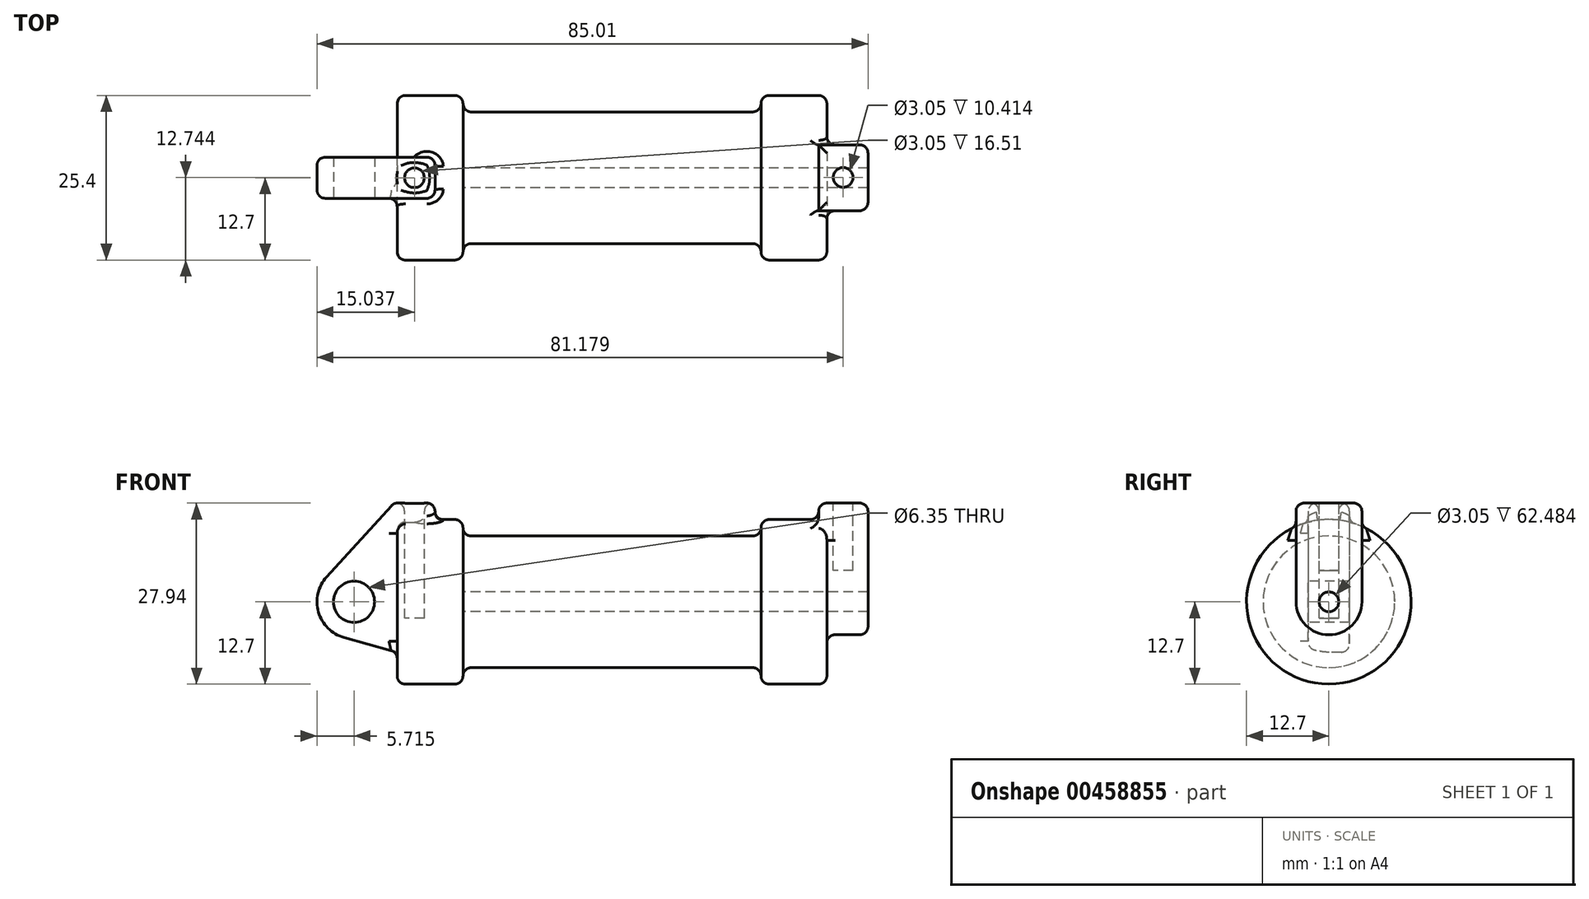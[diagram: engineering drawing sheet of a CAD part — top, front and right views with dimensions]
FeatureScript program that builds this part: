
annotation { "Feature Type Name" : "Feature", "Feature Type Description" : "" }
export const myFeature = defineFeature(function(context is Context, id is Id, definition is map)
    precondition{}
    {
        {
            var Q0;
            Q0=qCreatedBy(makeId("Front.planeOp"),FACE);
            var sketch = newSketch(context, id + "F0", { "sketchPlane" : qUnion([Q0])});
            skLineSegment(sketch, "E0", {"start": v(0, 0) * mm, "end": v(0, 12.7) * mm});
            skLineSegment(sketch, "E1", {"start": v(0, 12.7) * mm, "end": v(10.16, 12.7) * mm});
            skLineSegment(sketch, "E2", {"start": v(10.16, 12.7) * mm, "end": v(10.16, 10.16) * mm});
            skLineSegment(sketch, "E3", {"start": v(10.16, 10.16) * mm, "end": v(56.13, 10.16) * mm});
            skLineSegment(sketch, "E4", {"start": v(56.13, 10.16) * mm, "end": v(56.13, 12.7) * mm});
            skLineSegment(sketch, "E5", {"start": v(56.13, 12.7) * mm, "end": v(66.3, 12.7) * mm});
            skLineSegment(sketch, "E6", {"start": v(66.3, 12.7) * mm, "end": v(66.3, 0) * mm});
            skLineSegment(sketch, "E7", {"start": v(66.3, 0) * mm, "end": v(0, 0) * mm});
            skLineSegment(sketch, "E8", {"start": v(5.84, 15.24) * mm, "end": v(-0.5, 15.24) * mm});
            skLineSegment(sketch, "E9", {"start": v(-0.5, 15.24) * mm, "end": v(-10.88, 3.85) * mm});
            skLineSegment(sketch, "E10", {"start": v(0, 0) * mm, "end": v(-6.65, 0) * mm});
            skCircle(sketch, "E11", {"center": v(-6.65, 0) * mm, "radius": 5.72 * mm});
            skCircle(sketch, "E12", {"center": v(-6.65, 0) * mm, "radius": 3.18 * mm});
            skLineSegment(sketch, "E13", {"start": v(5.84, 15.24) * mm, "end": v(5.84, -9.4) * mm});
            skLineSegment(sketch, "E14", {"start": v(5.84, -9.4) * mm, "end": v(-8.18, -5.5) * mm});
            skSolve(sketch);
        }
        {
            var Q0;
            {var subQ0=sQuery(id+"F0.wireOp",EDGE,"E2");Q0=makeQuery(id+"F0.imprint","IMPRINT",FACE,{"disambiguationData":[TD([[makeQuery(id+"F0.imprint","IMPRINT",EDGE,{"derivedFrom":subQ0}),-1.0]])]});}
            var Q1;
            {var subQ0=sQuery(id+"F0.wireOp",EDGE,"E0");Q1=makeQuery(id+"F0.imprint","IMPRINT",FACE,{"disambiguationData":[TD([[makeQuery(id+"F0.imprint","IMPRINT",EDGE,{"derivedFrom":subQ0}),-1.0]])]});}
            var Q2;
            Q2=sQuery(id+"F0.wireOp",EDGE,"E7");
            revolve(context, id + "F1", {"entities" : qUnion([Q0, Q1]), "axis" : qUnion([Q2]), "revolveType" : RevolveType.FULL});
        }
        {
            var Q0;
            {var subQ1=sQuery(id+"F0.wireOp",EDGE,"E0");Q0=makeQuery(id+"F0.imprint","IMPRINT",FACE,{"disambiguationData":[TD([[makeQuery(id+"F0.imprint","IMPRINT",EDGE,{"derivedFrom":subQ1}),1.0]])]});}
            var Q1;
            {var subQ5=sQuery(id+"F0.wireOp",EDGE,"E12");Q1=makeQuery(id+"F0.imprint","IMPRINT",FACE,{"disambiguationData":[TD([[makeQuery(id+"F0.imprint","IMPRINT",EDGE,{"derivedFrom":subQ5}),-1.0]])]});}
            var Q2;
            {var subQ0=sQuery(id+"F0.wireOp",EDGE,"E14");Q2=makeQuery(id+"F0.imprint","IMPRINT",FACE,{"disambiguationData":[TD([[makeQuery(id+"F0.imprint","IMPRINT",EDGE,{"derivedFrom":subQ0}),-1.0]])]});}
            var Q3;
            {var subQ0=sQuery(id+"F0.wireOp",EDGE,"E0");Q3=makeQuery(id+"F0.imprint","IMPRINT",FACE,{"disambiguationData":[TD([[makeQuery(id+"F0.imprint","IMPRINT",EDGE,{"derivedFrom":subQ0}),-1.0]])]});}
            extrude(context, id + "F2", {"entities" : qUnion([Q0, Q1, Q2, Q3]), "operationType" : NewBodyOperationType.ADD, "oppositeDirection" : true, "depth" : 3.17 * mm, "hasSecondDirection" : true, "secondDirectionOppositeDirection" : false, "secondDirectionDepth" : 3.17 * mm});
        }
        {
            var Q0;
            Q0=makeQuery(id+"F1.opRevolve","SWEPT_FACE",FACE,{"disambiguationData":[OSD([sQuery(id+"F0.wireOp",EDGE,"E6")])]});
            var sketch = newSketch(context, id + "F3", { "sketchPlane" : qUnion([Q0])});
            skCircle(sketch, "E15", {"center": v(0, 0) * mm, "radius": 1.52 * mm});
            skCircle(sketch, "E16", {"center": v(0, 0) * mm, "radius": 5.08 * mm});
            skLineSegment(sketch, "E17", {"start": v(-5.08, 0) * mm, "end": v(-5.08, 15.24) * mm});
            skLineSegment(sketch, "E18", {"start": v(5.08, 0) * mm, "end": v(5.08, 15.24) * mm});
            skLineSegment(sketch, "E19", {"start": v(-5.08, 15.24) * mm, "end": v(5.08, 15.24) * mm});
            skSolve(sketch);
        }
        {
            var Q0;
            Q0=qSketchRegion(id+"F3",true);
            extrude(context, id + "F4", {"entities" : qUnion([Q0]), "operationType" : NewBodyOperationType.ADD, "depth" : 6.35 * mm, "hasSecondDirection" : true, "secondDirectionOppositeDirection" : true, "secondDirectionDepth" : 1.27 * mm});
        }
        {
            var Q0;
            Q0=makeQuery(id+"F3.imprint","IMPRINT",FACE,{"disambiguationData":[TD([[makeQuery(id+"F3.imprint","IMPRINT",EDGE,{"derivedFrom":sQuery(id+"F3.wireOp",EDGE,"E15")}),1.0]])]});
            var Q1;
            Q1=makeQuery(id+"F1.opRevolve","SWEPT_FACE",FACE,{"disambiguationData":[OSD([sQuery(id+"F0.wireOp",EDGE,"E2")])]});
            extrude(context, id + "F5", {"entities" : qUnion([Q0]), "operationType" : NewBodyOperationType.REMOVE, "endBound" : BoundingType.UP_TO_SURFACE, "oppositeDirection" : true, "endBoundEntityFace" : qUnion([Q1]), "depth" : 25.4 * mm});
        }
        {
            var Q0;
            Q0=makeQuery(id+"F4.opExtrude","SWEPT_FACE",FACE,{"disambiguationData":[OSD([sQuery(id+"F3.wireOp",EDGE,"E19")])]});
            var sketch = newSketch(context, id + "F6", { "sketchPlane" : qUnion([Q0])});
            skCircle(sketch, "E20", {"center": v(68.8, 0.04) * mm, "radius": 1.52 * mm});
            skSolve(sketch);
        }
        {
            var Q0;
            Q0=makeQuery(id+"F2.opExtrude","SWEPT_FACE",FACE,{"disambiguationData":[OSD([sQuery(id+"F0.wireOp",EDGE,"E8")])]});
            var sketch = newSketch(context, id + "F7", { "sketchPlane" : qUnion([Q0])});
            skCircle(sketch, "E21", {"center": v(2.67, 0) * mm, "radius": 1.52 * mm});
            skPoint(sketch, "E21.centerSnap0", {"position": v(5.84, 0) * mm});
            skSolve(sketch);
        }
        {
            var Q0;
            Q0 = qSketchRegion(id + "F6", true);
            extrude(context, id + "F8", {"entities" : qUnion([Q0]), "operationType" : NewBodyOperationType.REMOVE, "oppositeDirection" : true, "depth" : 10.4 * mm});
        }
        {
            var Q0;
            Q0 = qSketchRegion(id + "F7", true);
            extrude(context, id + "F9", {"entities" : qUnion([Q0]), "operationType" : NewBodyOperationType.REMOVE, "oppositeDirection" : true, "depth" : 17.78 * mm});
        }
        {
            var Q0;
            Q0=makeQuery(id+"F1.opRevolve","SWEPT_EDGE",EDGE,{"disambiguationData":[OSD([sQuery(id+"F0.wireOp",EDGE,"E1"),sQuery(id+"F0.wireOp",EDGE,"E2")])]});
            var Q1;
            Q1=makeQuery(id+"F1.opRevolve","SWEPT_EDGE",EDGE,{"disambiguationData":[OSD([sQuery(id+"F0.wireOp",EDGE,"E2"),sQuery(id+"F0.wireOp",EDGE,"E3")])]});
            var Q2;
            Q2=makeQuery(id+"F1.opRevolve","SWEPT_EDGE",EDGE,{"disambiguationData":[OSD([sQuery(id+"F0.wireOp",EDGE,"E4"),sQuery(id+"F0.wireOp",EDGE,"E5")])]});
            var Q3;
            Q3=makeQuery(id+"F1.opRevolve","SWEPT_EDGE",EDGE,{"disambiguationData":[OSD([sQuery(id+"F0.wireOp",EDGE,"E3"),sQuery(id+"F0.wireOp",EDGE,"E4")])]});
            var Q4;
            Q4=makeQuery(id+"F1.opRevolve","SWEPT_EDGE",EDGE,{"disambiguationData":[OSD([sQuery(id+"F0.wireOp",EDGE,"E5"),sQuery(id+"F0.wireOp",EDGE,"E6")])]});
            var Q5;
            Q5=makeQuery(id+"F1.opRevolve","SWEPT_EDGE",EDGE,{"disambiguationData":[OSD([sQuery(id+"F0.wireOp",EDGE,"E0"),sQuery(id+"F0.wireOp",EDGE,"E1")])]});
            fillet(context, id + "F10", {"entities" : qUnion([Q0, Q1, Q2, Q3, Q4, Q5]), "radius" : 1.27 * mm, "tangentPropagation" : true, "allowEdgeOverflow" : false});
        }
        {
            var Q0;
            Q0=makeQuery(id+"F4.opExtrude","CAP_EDGE",EDGE,{"disambiguationData":[OSD([sQuery(id+"F3.wireOp",EDGE,"E18")])],"isStart":false});
            var Q1;
            Q1=makeQuery(id+"F4.boolean.opBoolean","INTERSECT",EDGE,{"derivedFrom":[makeQuery(id+"F1.opRevolve","SWEPT_FACE",FACE,{"disambiguationData":[OSD([sQuery(id+"F0.wireOp",EDGE,"E6")])]}),makeQuery(id+"F4.opExtrude","SWEPT_FACE",FACE,{"disambiguationData":[OSD([sQuery(id+"F3.wireOp",EDGE,"E18")])]})]});
            var Q2;
            Q2=makeQuery(id+"F4.boolean.opBoolean","INTERSECT",EDGE,{"derivedFrom":[makeQuery(id+"F1.opRevolve","SWEPT_FACE",FACE,{"disambiguationData":[OSD([sQuery(id+"F0.wireOp",EDGE,"E5")])]}),makeQuery(id+"F4.opExtrude","CAP_FACE",FACE,{"disambiguationData":[OSD([sQuery(id+"F3.wireOp",EDGE,"E15"),sQuery(id+"F3.wireOp",EDGE,"E16"),sQuery(id+"F3.wireOp",EDGE,"E17"),sQuery(id+"F3.wireOp",EDGE,"E18"),sQuery(id+"F3.wireOp",EDGE,"E19")])],"isStart":true})]});
            var Q3;
            Q3=makeQuery(id+"F4.opExtrude","CAP_EDGE",EDGE,{"disambiguationData":[OSD([sQuery(id+"F3.wireOp",EDGE,"E19")])],"isStart":true});
            var Q4;
            Q4=makeQuery(id+"F4.opExtrude","SWEPT_EDGE",EDGE,{"disambiguationData":[OSD([sQuery(id+"F3.wireOp",EDGE,"E18"),sQuery(id+"F3.wireOp",EDGE,"E19")])]});
            var Q5;
            Q5=makeQuery(id+"F4.opExtrude","CAP_EDGE",EDGE,{"disambiguationData":[OSD([sQuery(id+"F3.wireOp",EDGE,"E19")])],"isStart":false});
            var Q6;
            Q6=makeQuery(id+"F4.opExtrude","SWEPT_EDGE",EDGE,{"disambiguationData":[OSD([sQuery(id+"F3.wireOp",EDGE,"E17"),sQuery(id+"F3.wireOp",EDGE,"E19")])]});
            fillet(context, id + "F11", {"entities" : qUnion([Q0, Q1, Q2, Q3, Q4, Q5, Q6]), "radius" : 1.27 * mm, "tangentPropagation" : true, "allowEdgeOverflow" : false});
        }
        {
            var Q0;
            Q0=makeQuery(id+"F2.boolean.opBoolean","INTERSECT",EDGE,{"derivedFrom":[makeQuery(id+"F1.opRevolve","SWEPT_FACE",FACE,{"disambiguationData":[OSD([sQuery(id+"F0.wireOp",EDGE,"E0")])]}),makeQuery(id+"F2.opExtrude","CAP_FACE",FACE,{"disambiguationData":[OSD([sQuery(id+"F0.wireOp",EDGE,"E8"),sQuery(id+"F0.wireOp",EDGE,"E9"),sQuery(id+"F0.wireOp",EDGE,"E11"),sQuery(id+"F0.wireOp",EDGE,"E12"),sQuery(id+"F0.wireOp",EDGE,"E13"),sQuery(id+"F0.wireOp",EDGE,"E14")])],"isStart":true})]});
            var Q1;
            Q1=makeQuery(id+"F2.opExtrude","CAP_EDGE",EDGE,{"disambiguationData":[OSD([sQuery(id+"F0.wireOp",EDGE,"E9")])],"isStart":true});
            var Q2;
            Q2=makeQuery(id+"F2.opExtrude","CAP_EDGE",EDGE,{"disambiguationData":[OSD([sQuery(id+"F0.wireOp",EDGE,"E11")])],"isStart":true});
            var Q3;
            Q3=makeQuery(id+"F2.opExtrude","CAP_EDGE",EDGE,{"disambiguationData":[OSD([sQuery(id+"F0.wireOp",EDGE,"E11")])],"isStart":false});
            var Q4;
            Q4=makeQuery(id+"F2.opExtrude","SWEPT_EDGE",EDGE,{"disambiguationData":[OSD([sQuery(id+"F0.wireOp",EDGE,"E8"),sQuery(id+"F0.wireOp",EDGE,"E13")])]});
            var Q5;
            Q5=makeQuery(id+"F2.opExtrude","CAP_EDGE",EDGE,{"disambiguationData":[OSD([sQuery(id+"F0.wireOp",EDGE,"E8")])],"isStart":false});
            var Q6;
            Q6=makeQuery(id+"F2.opExtrude","SWEPT_FACE",FACE,{"disambiguationData":[OSD([sQuery(id+"F0.wireOp",EDGE,"E8")])]});
            var Q7;
            Q7=makeQuery(id+"F2.boolean.opBoolean","INTERSECT",EDGE,{"derivedFrom":[makeQuery(id+"F1.opRevolve","SWEPT_FACE",FACE,{"disambiguationData":[OSD([sQuery(id+"F0.wireOp",EDGE,"E1")])]}),makeQuery(id+"F2.opExtrude","SWEPT_FACE",FACE,{"disambiguationData":[OSD([sQuery(id+"F0.wireOp",EDGE,"E13")])]})]});
            var Q8;
            Q8=makeQuery(id+"F2.opExtrude","CAP_EDGE",EDGE,{"disambiguationData":[OSD([sQuery(id+"F0.wireOp",EDGE,"E13")])],"isStart":false});
            var Q9;
            Q9=makeQuery(id+"F2.opExtrude","CAP_EDGE",EDGE,{"disambiguationData":[OSD([sQuery(id+"F0.wireOp",EDGE,"E13")])],"isStart":true});
            fillet(context, id + "F12", {"entities" : qUnion([Q0, Q1, Q2, Q3, Q4, Q5, Q6, Q7, Q8, Q9]), "radius" : 1.27 * mm, "tangentPropagation" : true, "allowEdgeOverflow" : false});
        }
    });
